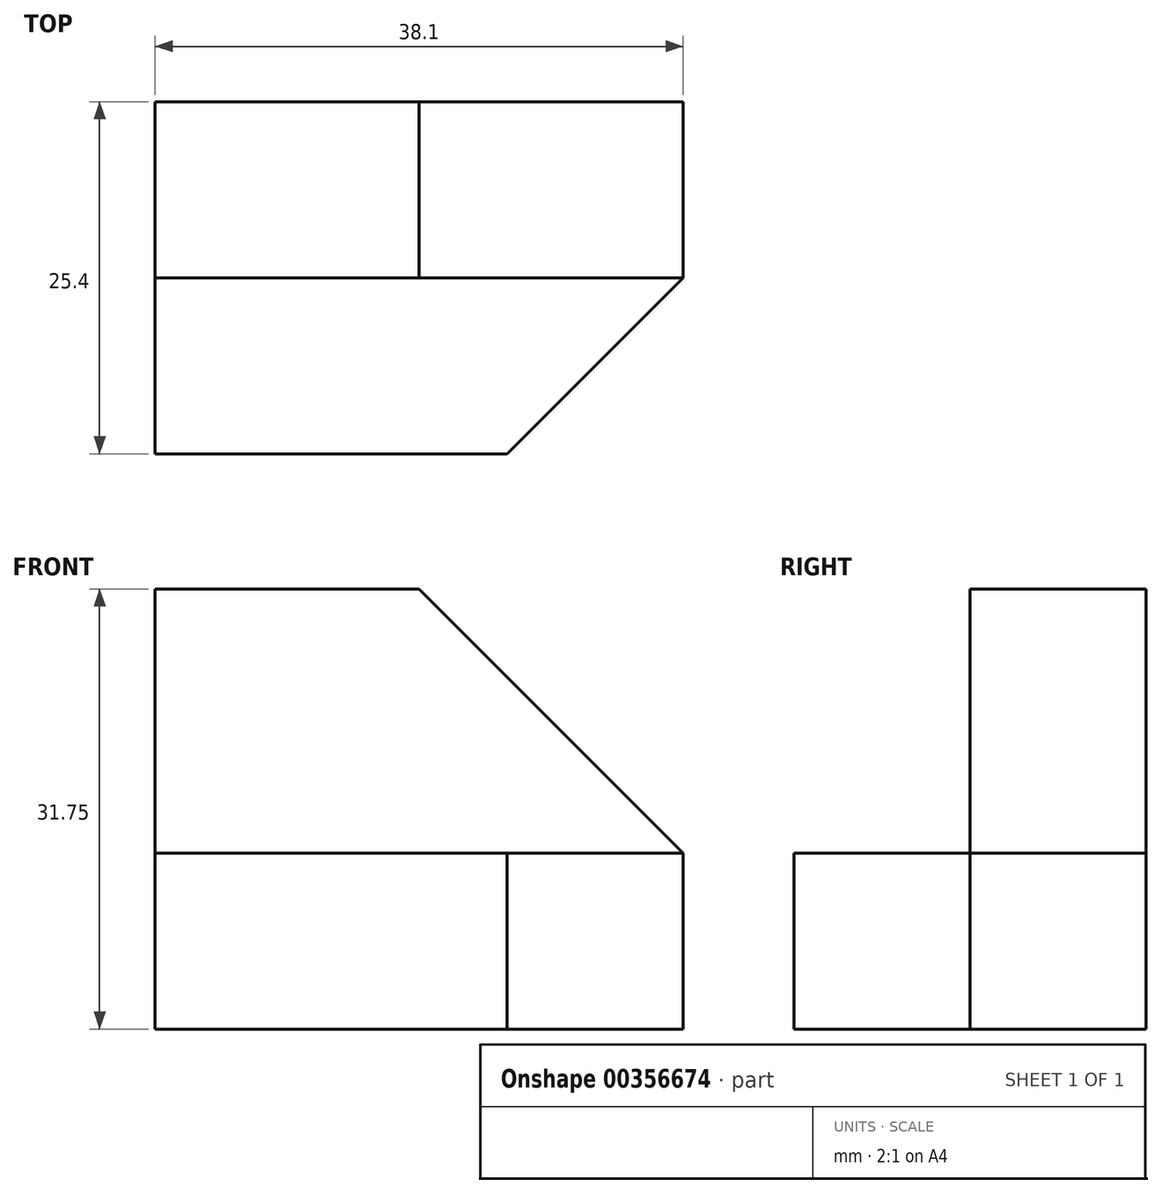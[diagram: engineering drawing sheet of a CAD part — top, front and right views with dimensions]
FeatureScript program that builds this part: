
annotation { "Feature Type Name" : "Feature", "Feature Type Description" : "" }
export const myFeature = defineFeature(function(context is Context, id is Id, definition is map)
    precondition{}
    {
        {
            var Q0;
            Q0=qCreatedBy(makeId("Front.planeOp"),FACE);
            var sketch = newSketch(context, id + "F0", { "sketchPlane" : qUnion([Q0])});
            skLineSegment(sketch, "E0", {"start": v(-31.12, -28.58) * mm, "end": v(6.98, -28.58) * mm});
            skLineSegment(sketch, "E1", {"start": v(6.98, -28.58) * mm, "end": v(6.98, 3.17) * mm});
            skLineSegment(sketch, "E2", {"start": v(6.98, 3.17) * mm, "end": v(-31.12, 3.17) * mm});
            skLineSegment(sketch, "E3", {"start": v(-31.12, 3.17) * mm, "end": v(-31.12, -28.58) * mm});
            skSolve(sketch);
        }
        {
            var Q0;
            Q0=makeQuery(id+"F0.imprint","IMPRINT",FACE,{"disambiguationData":[TD([[makeQuery(id+"F0.imprint","IMPRINT",EDGE,{"derivedFrom":sQuery(id+"F0.wireOp",EDGE,"E0")}),1.0]])]});
            extrude(context, id + "F1", {"entities" : qUnion([Q0]), "depth" : 25.4 * mm});
        }
        {
            var Q0;
            Q0=makeQuery(id+"F1.opExtrude","SWEPT_FACE",FACE,{"disambiguationData":[OSD([sQuery(id+"F0.wireOp",EDGE,"E2")])]});
            var sketch = newSketch(context, id + "F2", { "sketchPlane" : qUnion([Q0])});
            skLineSegment(sketch, "E4", {"start": v(-31.12, -12.7) * mm, "end": v(6.98, -12.7) * mm});
            skLineSegment(sketch, "E5", {"start": v(6.98, -12.7) * mm, "end": v(6.98, -25.4) * mm});
            skLineSegment(sketch, "E6", {"start": v(6.98, -25.4) * mm, "end": v(-31.12, -25.4) * mm});
            skLineSegment(sketch, "E7", {"start": v(-31.12, -25.4) * mm, "end": v(-31.12, -12.7) * mm});
            skSolve(sketch);
        }
        {
            var Q0;
            Q0=makeQuery(id+"F2.imprint","IMPRINT",FACE,{"disambiguationData":[TD([[makeQuery(id+"F2.imprint","IMPRINT",EDGE,{"derivedFrom":sQuery(id+"F2.wireOp",EDGE,"E4")}),-1.0]])]});
            extrude(context, id + "F3", {"entities" : qUnion([Q0]), "operationType" : NewBodyOperationType.REMOVE, "oppositeDirection" : true, "depth" : 19.05 * mm});
        }
        {
            var Q0;
            Q0=makeQuery(id+"F3.boolean.opBoolean","COPY",FACE,{"derivedFrom":makeQuery(id+"F3.opExtrude","CAP_FACE",FACE,{"disambiguationData":[OSD([sQuery(id+"F2.wireOp",EDGE,"E4"),sQuery(id+"F2.wireOp",EDGE,"E5"),sQuery(id+"F2.wireOp",EDGE,"E6"),sQuery(id+"F2.wireOp",EDGE,"E7")])],"isStart":false})});
            var sketch = newSketch(context, id + "F4", { "sketchPlane" : qUnion([Q0])});
            skLineSegment(sketch, "E8", {"start": v(-5.72, -25.4) * mm, "end": v(6.98, -12.7) * mm});
            skLineSegment(sketch, "E9", {"start": v(6.98, -12.7) * mm, "end": v(6.98, -25.4) * mm});
            skLineSegment(sketch, "E10", {"start": v(6.98, -25.4) * mm, "end": v(-5.72, -25.4) * mm});
            skSolve(sketch);
        }
        {
            var Q0;
            Q0=makeQuery(id+"F4.imprint","IMPRINT",FACE,{"disambiguationData":[TD([[makeQuery(id+"F4.imprint","IMPRINT",EDGE,{"derivedFrom":sQuery(id+"F4.wireOp",EDGE,"E8")}),-1.0]])]});
            extrude(context, id + "F5", {"entities" : qUnion([Q0]), "operationType" : NewBodyOperationType.REMOVE, "oppositeDirection" : true, "depth" : 25.4 * mm});
        }
        {
            var Q0;
            Q0=makeQuery(id+"F3.boolean.opBoolean","COPY",FACE,{"derivedFrom":makeQuery(id+"F3.opExtrude","SWEPT_FACE",FACE,{"disambiguationData":[OSD([sQuery(id+"F2.wireOp",EDGE,"E4")])]})});
            var sketch = newSketch(context, id + "F6", { "sketchPlane" : qUnion([Q0])});
            skLineSegment(sketch, "E11", {"start": v(-12.07, 3.17) * mm, "end": v(6.98, -15.88) * mm});
            skLineSegment(sketch, "E12", {"start": v(6.98, -15.88) * mm, "end": v(6.98, 3.17) * mm});
            skLineSegment(sketch, "E13", {"start": v(6.98, 3.17) * mm, "end": v(-12.07, 3.17) * mm});
            skSolve(sketch);
        }
        {
            var Q0;
            Q0=makeQuery(id+"F6.imprint","IMPRINT",FACE,{"disambiguationData":[TD([[makeQuery(id+"F6.imprint","IMPRINT",EDGE,{"derivedFrom":sQuery(id+"F6.wireOp",EDGE,"E11")}),1.0]])]});
            extrude(context, id + "F7", {"entities" : qUnion([Q0]), "operationType" : NewBodyOperationType.REMOVE, "oppositeDirection" : true, "depth" : 25.4 * mm});
        }
    });
